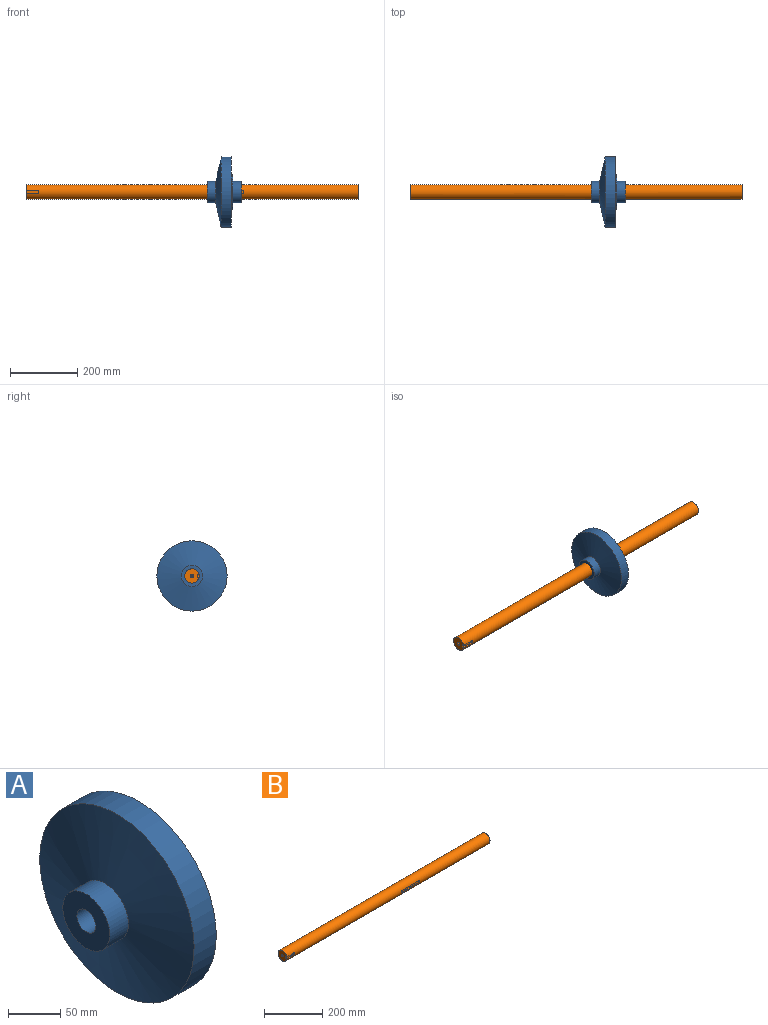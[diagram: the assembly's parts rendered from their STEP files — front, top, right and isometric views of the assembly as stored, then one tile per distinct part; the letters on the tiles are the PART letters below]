
ASSEMBLY  parts=2 mates=1
PART A: 10 faces, bbox 101.6x209.6x209.6 mm
  f0: cylinder r=104.77mm len=209.55mm, axis (1,0,0), area 19748.5mm2, adj f1,f9
  f1: cone r=104.77mm half-angle=77.5deg, axis (1,0,0), area 32082.6mm2, adj f0,f2
  f2: cylinder r=31.75mm len=63.5mm, axis (1,0,0), area 5067.1mm2, adj f1,f3
  f3: plane 63.5x63.5mm, normal (-1,0,0), area 2660.2mm2, adj f2,f4
  f4: cylinder r=12.7mm len=101.6mm, axis (1,0,0), area 8107.3mm2, adj f3,f5
  f5: plane 63.5x63.5mm, normal (1,0,0), area 2660.2mm2, adj f4,f6
  f6: cylinder r=31.75mm len=63.5mm, axis (1,0,0), area 5067.1mm2, adj f5,f7
  f7: plane 106.95x106.95mm, normal (1,0,0), area 5817.4mm2, adj f6,f8
  f8: cylinder r=53.48mm len=106.95mm, axis (1,0,0), area 1545mm2, adj f7,f9
  f9: plane 209.55x209.55mm, normal (1,0,0), area 25503.5mm2, adj f0,f8
PART B: 24 faces, bbox 990.6x42.8x42.8 mm
  f0: cylinder r=21.41mm len=990.6mm, axis (1,0,0), area 132057.1mm2, adj f1,f2,f9,f11,f12,f13,f14,f15
  f1: plane 42.82x42.29mm, normal (-1,0,0), area 1322.2mm2, adj f0,f3,f9,f10,f11
  f2: plane 42.82x42.82mm, normal (1,0,0), area 1369.1mm2, adj f0,f8
  f3: cone r=4.76mm half-angle=30deg, axis (-1,0,0), area 117.8mm2, adj f1,f4
  f4: cylinder r=1.98mm len=9.02mm, axis (1,0,0), area 112.2mm2, adj f3,f5
  f5: plane 3.96x3.96mm, normal (-1,0,0), area 12.3mm2, adj f4
  f6: plane 3.96x3.96mm, normal (1,0,0), area 12.3mm2, adj f7
  f7: cylinder r=1.98mm len=9.02mm, axis (1,0,0), area 112.2mm2, adj f6,f8
  f8: cone r=4.76mm half-angle=30deg, axis (1,0,0), area 117.8mm2, adj f2,f7
  f9: plane 33.38x4.57mm, normal (0,0,-1), area 152.5mm2, adj f0,f1,f10,f13
  f10: plane 38.1x9.53mm, normal (0,-1,0), area 353.3mm2, adj f1,f9,f11,f12,f13,f14
  f11: plane 33.38x4.57mm, normal (0,0,1), area 152.5mm2, adj f0,f1,f10,f14
  f12: plane 5.11x0.08mm, normal (-1,0,0), area 0.4mm2, adj f0,f10,f13,f14
  f13: cylinder r=4.72mm len=5.11mm, axis (0,1,0), area 35.9mm2, adj f0,f9,f10,f12
  f14: cylinder r=4.72mm len=5.11mm, axis (0,-1,0), area 35.9mm2, adj f0,f10,f11,f12
  f15: plane 81.99x3.54mm, normal (0,0,-1), area 290.3mm2, adj f0,f19,f20,f23
  f16: plane 4.08x0.08mm, normal (1,0,0), area 0.3mm2, adj f0,f19,f20,f21
  f17: plane 81.99x3.54mm, normal (0,0,1), area 290.3mm2, adj f0,f19,f21,f22
  f18: plane 4.08x0.08mm, normal (-1,0,0), area 0.3mm2, adj f0,f19,f22,f23
  f19: plane 91.44x9.53mm, normal (0,-1,0), area 851.8mm2, adj f15,f16,f17,f18,f20,f21,f22,f23
  f20: cylinder r=4.72mm len=4.72mm, axis (0,-1,0), area 28.3mm2, adj f0,f15,f16,f19
  f21: cylinder r=4.72mm len=4.72mm, axis (0,1,0), area 28.3mm2, adj f0,f16,f17,f19
  f22: cylinder r=4.72mm len=4.72mm, axis (0,-1,0), area 28.3mm2, adj f0,f17,f18,f19
  f23: cylinder r=4.72mm len=4.72mm, axis (0,1,0), area 28.3mm2, adj f0,f15,f18,f19
PLACE A t=(-359.81,-188.21,130.63)mm
PLACE B t=(18.47,-188.21,130.63)mm
MATE planar A.f0 <-> B.f0  axis (1,0,0) through (-359.81,-188.21,130.63)mm
